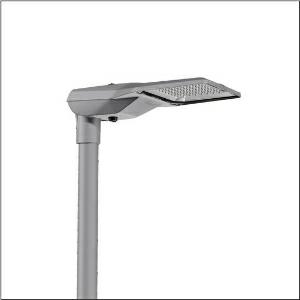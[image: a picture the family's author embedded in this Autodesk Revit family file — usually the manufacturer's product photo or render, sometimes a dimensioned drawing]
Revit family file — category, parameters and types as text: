
# Revit family: streetlight_sl_21_midi___pl52_5xe3h43t08lb_3b1c
name_source: partatom
category: Lighting Fixtures
units: mm (PartAtom-declared; Revit-internal decimal feet)

## family parameters
Cut with Voids When Loaded = No
Host = Face
Light Source = No
Part Type = Normal
Room Calculation Point = No
Round Connector Dimension = Use Diameter
Shared = No

## types (1)
- --- (1 x LED, 14690 lm, 99.6 W, 4000K)
    Apparent Load = 100 VA
    CIE Flux Codes = 27 59 98 100 100
    Color Rendering = 70
    Color Temperature = 4000K
    Default Elevation = 1800 mm
    Description = Streetlight SL 21 midi, mast luminaire, primary light control with lens, of PMMA, primary optical cover: cover, of toughened safety glass, transparent, light distribution: PL52, light emission: direct distribution, primary light characteristic: asymmetric, installation type: side-entry, post-top, LED, High Power LED, rated luminous flux: 14.690lm, luminous efficacy: 148lm/W, light colour: 740, colour temperature: 4000K, control gear: D4i, control: overheat protection, constant luminous flux control, time-dependent luminous flux control, flexible luminous flux parameterisation, pre-setting: logarithmic dimming characteristic, mains connection: 230..240V, AC, 50/60Hz, start of lifetime: 100W, end of service life: 102W, reduction: 46W, luminaire housing, of diecast aluminium, powder-coated, Siteco® metallic grey (DB 702S), corrosivity category C5 mid according to DIN EN ISO 12944, please order mast flange separately, inclination adjustable: 0°, 5°, 10°, 15°, sealing non-destructively replaceable, multi-level sealing system, length: 644mm, width: 335mm, height: 110mm, mast flange for spigot size: 42mm (side-entry): 5XC10008XM4, 60/48mm (side-entry/post-top): 5XC10108XM2, 76/60mm (side-entry/post-top): 5XC10108XM1, mounting height: 4..8m, Smart Interface below and above, protection rating (complete): IP66, insulation class (complete): insulation class II (safety insulation), certification: CE, ENEC, ENEC+, VDE, impact resistance: IK10, permissible operating ambient temperature for outdoor applications: -40..+50°C, standard-compliant lighting for roads and squares, packaging unit: 1 piece

Light Distribution: PL52
    Height = 111 mm
    Lamp = 1 x LED
    Lamp Light Flux = 14690 lm
    Lamp Power = 99.6 W
    Lamp count = 1
    Length = 644 mm
    Luminous efficacy = 147 lm/W
    Manufacturer = Siteco
    ModVariant = No
    Model = 5XE3H43T08LB
    Number of Poles = 1
    OnlyDefault = Yes
    Power Factor = 1
    Product Name = Streetlight SL 21 midi | PL52
    Product group = mast luminaire | pylon top
    ProductGroupID = 6100
    Protection Class = Protection class II
    Protection Degree = IP 66
    RLX_Detail_Level = 1
    RLX_Emergency_Light_Flux = 0 lm
    RLX_Emergency_Type = 0
    RLX_Emergency_Type_DB = No
    RlxData = <blob elided: 36509 chars, md5=00fae744>
    Socket = socket
    Standby Power = 0 W
    System Light Flux = 14690 lm
    System Power = 100 W
    Type Comments = factory setting: luminous flux: 100 % | dim-lin: 254 | 1020 mA
    Type Image = l_1004304.jpg
    URL = http://relux.com
    VarID = @adj_032313
    Voltage = 0 V
    Weight = 0.00 kg
    Width = 336 mm

## geometry (parser evidence)
native form markers: Blend x4, Sweep x10
no freeform markers — native parametric forms only
